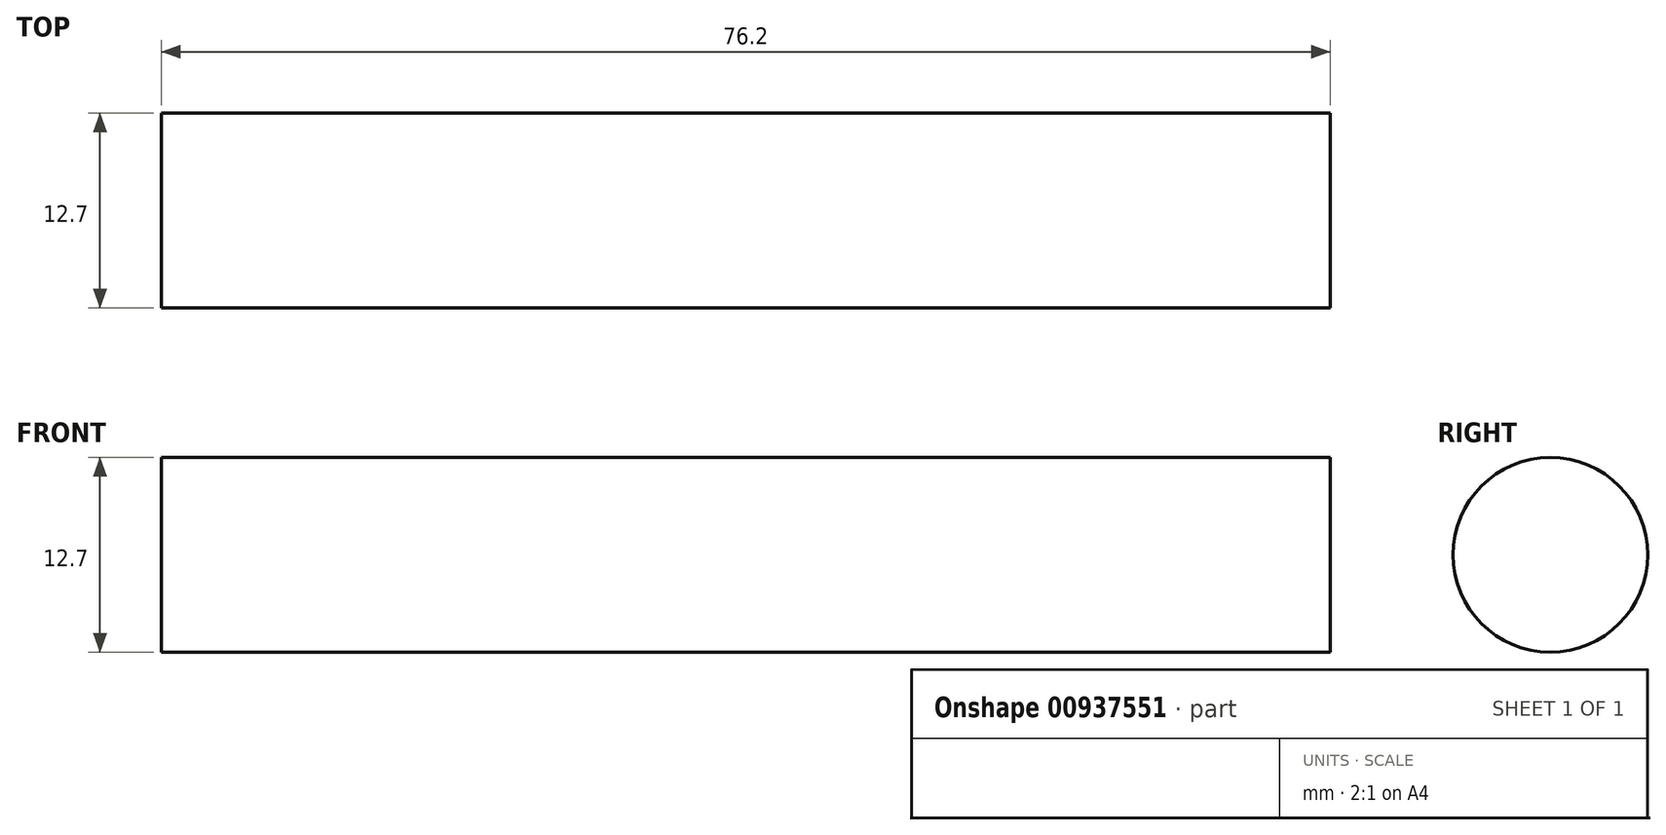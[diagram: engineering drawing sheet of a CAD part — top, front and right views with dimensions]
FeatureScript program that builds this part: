
annotation { "Feature Type Name" : "Feature", "Feature Type Description" : "" }
export const myFeature = defineFeature(function(context is Context, id is Id, definition is map)
    precondition{}
    {
        {
            var Q0;
            Q0=qCreatedBy(makeId("Right.planeOp"),FACE);
            var sketch = newSketch(context, id + "F0", { "sketchPlane" : qUnion([Q0])});
            skCircle(sketch, "E0", {"center": v(-44.95, 23.62) * mm, "radius": 6.35 * mm});
            skSolve(sketch);
        }
        {
            var Q0;
            Q0=makeQuery(id+"F0.imprint","IMPRINT",FACE,{"disambiguationData":[TD([[makeQuery(id+"F0.imprint","IMPRINT",EDGE,{"derivedFrom":sQuery(id+"F0.wireOp",EDGE,"E0")}),1.0]])]});
            extrude(context, id + "F1", {"entities" : qUnion([Q0]), "depth" : 38.1 * mm, "offsetDistance" : 25.4 * mm, "hasSecondDirection" : true, "secondDirectionOppositeDirection" : true, "secondDirectionDepth" : 38.1 * mm});
        }
    });
